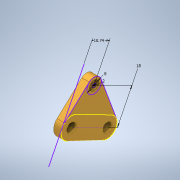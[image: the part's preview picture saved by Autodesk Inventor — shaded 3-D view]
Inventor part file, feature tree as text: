
AUTODESK INVENTOR PART (.ipt)
format: ipt  version: 2020 (Build 240168000, 168)  size: 153,600 bytes
history: native  units: in
note: dims shown in document units (in); Inventor stores cm internally (conversion verified against a paired STEP export)
features: extrude x3, sketch x3, projected_geometry x1
ambient origin geometry x8: Origin, YZ Plane, XZ Plane, XY Plane, X Axis, Y Axis, Z Axis, Center Point
bodies: Solid1 (feature_tree)
feature tree (7):
  extrude  "Extrusion1"  Depth=0.4523in
  extrude  "edit this sketch"  Depth=0.2118in
  extrude  "Extrusion3"  Depth=0.1575in TaperAngle=0.0deg
  sketch  "Sketch1"  dims[d0=0.2008in d1=0.2008in d3=0.4523in]
  sketch  "Sketch2"  dims[d4=0.2118in d5=0.8586in]
  projected_geometry  "Projected Loop1"
  sketch  "Sketch3"  dims[d6=0.8656in d7=0.1575in d8=0.0in d11=0.0787in d12=0.315in d13=0.1575in d14=0.0in d15=0.1969in d16=0.0787in d17=0.0in d20=0.7087in d21=0.4228in]
